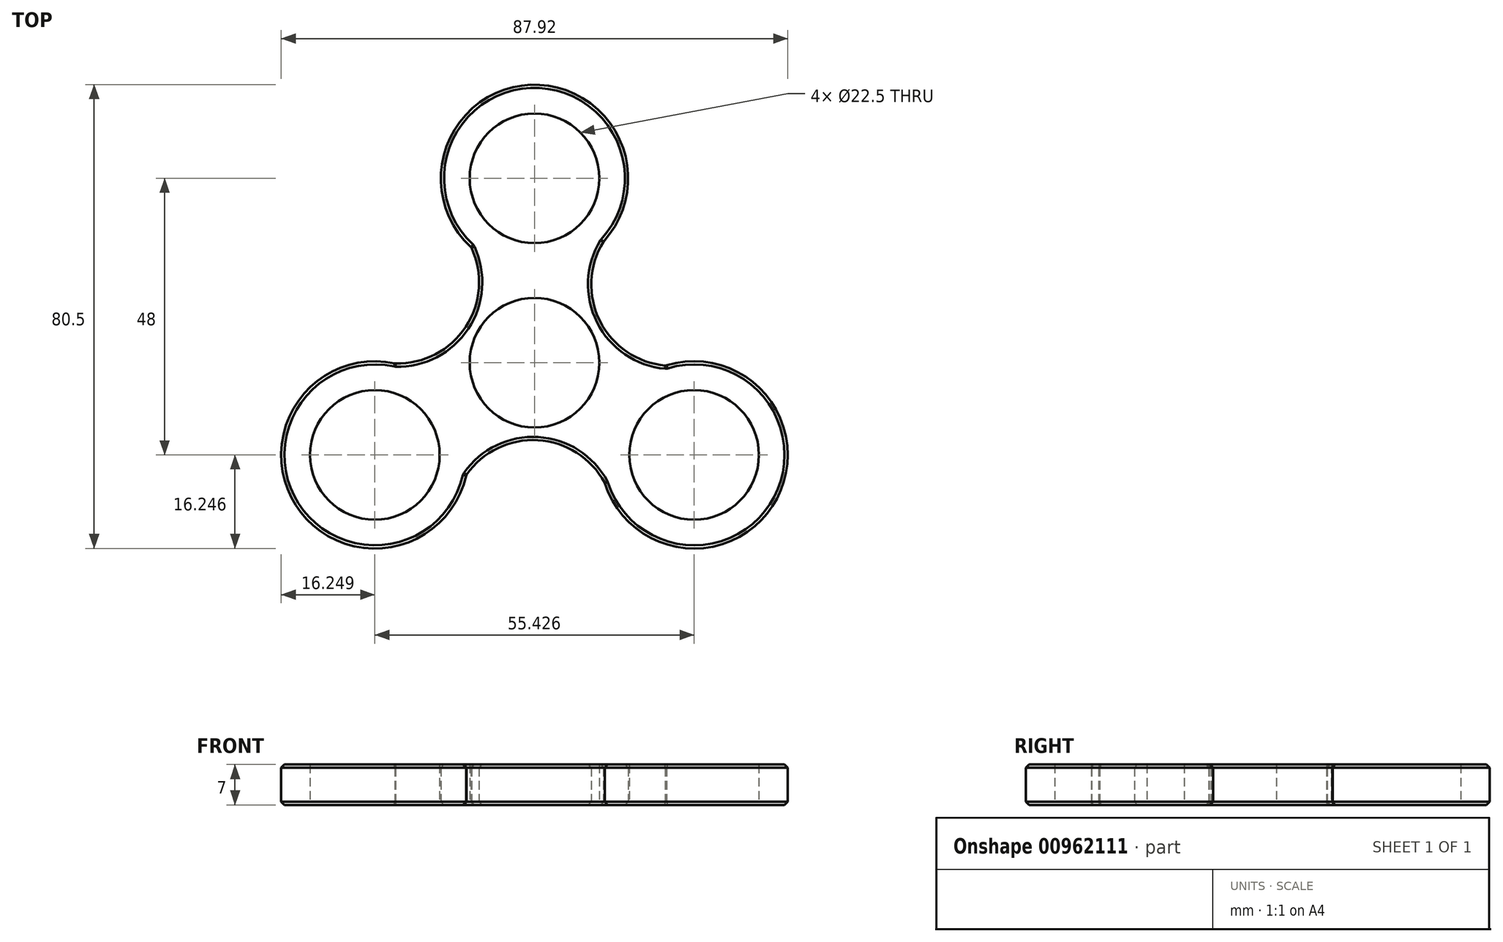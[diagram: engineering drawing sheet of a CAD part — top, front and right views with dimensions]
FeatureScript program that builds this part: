
annotation { "Feature Type Name" : "Feature", "Feature Type Description" : "" }
export const myFeature = defineFeature(function(context is Context, id is Id, definition is map)
    precondition{}
    {
        {
            var Q0;
            Q0=qCreatedBy(makeId("Top.planeOp"),FACE);
            var sketch = newSketch(context, id + "F0", { "sketchPlane" : qUnion([Q0])});
            skCircle(sketch, "E0", {"center": v(-33.54, -5.26) * mm, "radius": 11.25 * mm});
            skCircle(sketch, "E1", {"center": v(-33.54, 26.74) * mm, "radius": 11.25 * mm});
            skCircle(sketch, "E2.1.0", {"center": v(-61.25, -21.26) * mm, "radius": 11.25 * mm});
            skCircle(sketch, "E2.2.0", {"center": v(-5.83, -21.26) * mm, "radius": 11.25 * mm});
            skCircle(sketch, "E3.0", {"center": v(-33.54, 26.74) * mm, "radius": 16.25 * mm});
            skCircle(sketch, "E4.0", {"center": v(-61.25, -21.26) * mm, "radius": 16.25 * mm});
            skCircle(sketch, "E5.0", {"center": v(-5.83, -21.26) * mm, "radius": 16.25 * mm});
            skArc(sketch, "E6", {"start": v(-57.71, -5.4) * mm, "mid": v(-45.47, 0.97) * mm, "end": v(-44.51, 14.75) * mm});
            skArc(sketch, "E7.1.0", {"start": v(-21.33, -26.13) * mm, "mid": v(-32.98, -18.71) * mm, "end": v(-45.38, -24.77) * mm});
            skArc(sketch, "E7.2.0", {"start": v(-21.57, 15.74) * mm, "mid": v(-22.17, 1.95) * mm, "end": v(-10.72, -5.77) * mm});
            skSolve(sketch);
        }
        {
            var Q0;
            Q0=makeQuery(id+"F0.imprint","IMPRINT",FACE,{"disambiguationData":[TD([[makeQuery(id+"F0.imprint","IMPRINT",EDGE,{"derivedFrom":sQuery(id+"F0.wireOp",EDGE,"E0")}),-1.0]])]});
            var Q1;
            Q1=makeQuery(id+"F0.imprint","IMPRINT",FACE,{"disambiguationData":[TD([[makeQuery(id+"F0.imprint","IMPRINT",EDGE,{"derivedFrom":sQuery(id+"F0.wireOp",EDGE,"E2.1.0")}),-1.0]])]});
            var Q2;
            Q2=makeQuery(id+"F0.imprint","IMPRINT",FACE,{"disambiguationData":[TD([[makeQuery(id+"F0.imprint","IMPRINT",EDGE,{"derivedFrom":sQuery(id+"F0.wireOp",EDGE,"E2.2.0")}),-1.0]])]});
            var Q3;
            Q3=makeQuery(id+"F0.imprint","IMPRINT",FACE,{"disambiguationData":[TD([[makeQuery(id+"F0.imprint","IMPRINT",EDGE,{"derivedFrom":sQuery(id+"F0.wireOp",EDGE,"E1")}),-1.0]])]});
            extrude(context, id + "F1", {"entities" : qUnion([Q0, Q1, Q2, Q3]), "depth" : 7 * mm, "offsetDistance" : 25 * mm});
        }
        {
            var Q0;
            Q0=makeQuery(id+"F1.opExtrude","SWEPT_FACE",FACE,{"disambiguationData":[OSD([sQuery(id+"F0.wireOp",EDGE,"E3.0")])]});
            var Q1;
            Q1=makeQuery(id+"F1.opExtrude","SWEPT_FACE",FACE,{"disambiguationData":[OSD([sQuery(id+"F0.wireOp",EDGE,"E6")])]});
            var Q2;
            Q2=makeQuery(id+"F1.opExtrude","SWEPT_FACE",FACE,{"disambiguationData":[OSD([sQuery(id+"F0.wireOp",EDGE,"E4.0")])]});
            var Q3;
            Q3=makeQuery(id+"F1.opExtrude","SWEPT_FACE",FACE,{"disambiguationData":[OSD([sQuery(id+"F0.wireOp",EDGE,"E7.1.0")])]});
            var Q4;
            Q4=makeQuery(id+"F1.opExtrude","SWEPT_FACE",FACE,{"disambiguationData":[OSD([sQuery(id+"F0.wireOp",EDGE,"E5.0")])]});
            var Q5;
            Q5=makeQuery(id+"F1.opExtrude","SWEPT_FACE",FACE,{"disambiguationData":[OSD([sQuery(id+"F0.wireOp",EDGE,"E7.2.0")])]});
            chamfer(context, id + "F2", {"entities" : qUnion([Q0, Q1, Q2, Q3, Q4, Q5]), "width" : 0.55 * mm, "tangentPropagation" : true});
        }
    });
